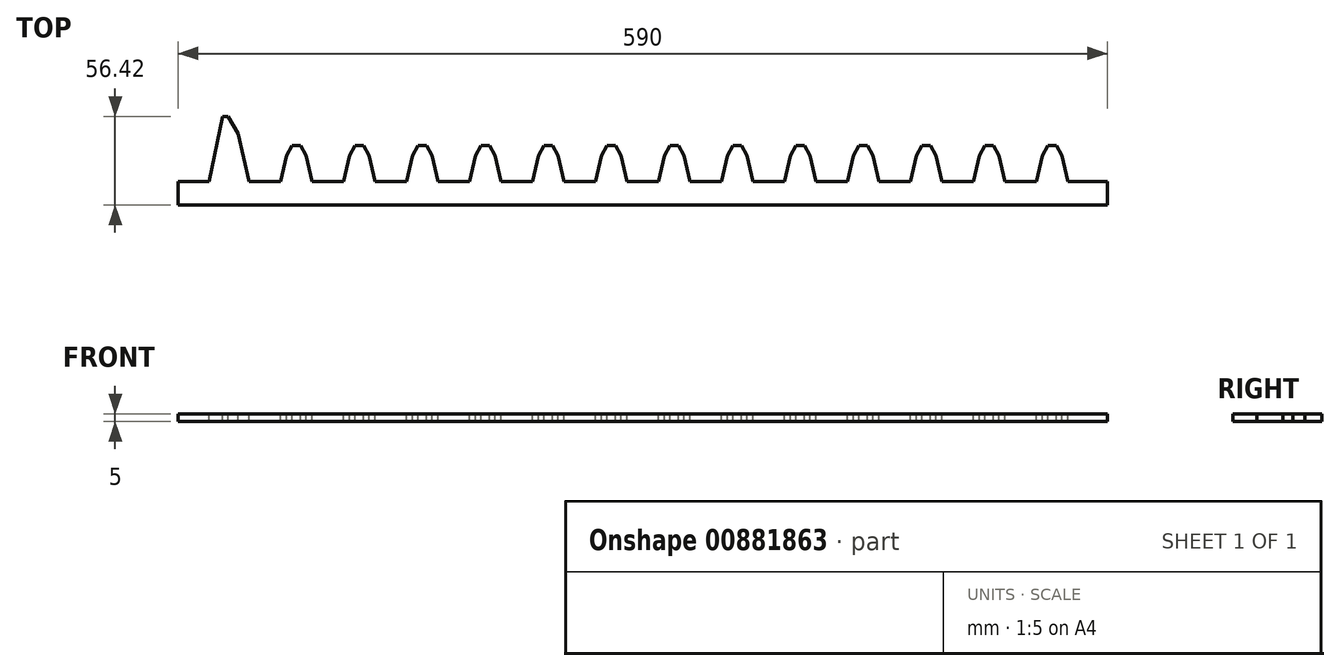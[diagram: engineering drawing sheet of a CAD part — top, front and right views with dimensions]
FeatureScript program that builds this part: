
annotation { "Feature Type Name" : "Feature", "Feature Type Description" : "" }
export const myFeature = defineFeature(function(context is Context, id is Id, definition is map)
    precondition{}
    {
        {
            var Q0;
            Q0=qCreatedBy(makeId("Top.planeOp"),FACE);
            var sketch = newSketch(context, id + "F0", { "sketchPlane" : qUnion([Q0])});
            skLineSegment(sketch, "E0.bottom", {"start": v(375, -330) * mm, "end": v(-375, -330) * mm});
            skLineSegment(sketch, "E0.top", {"start": v(375, 330) * mm, "end": v(-375, 330) * mm});
            skLineSegment(sketch, "E0.left", {"start": v(375, -330) * mm, "end": v(375, -280) * mm});
            skLineSegment(sketch, "E0.right", {"start": v(-375, -330) * mm, "end": v(-375, -280) * mm});
            skPoint(sketch, "E0.middle", {"position": v(0, 0) * mm});
            skLineSegment(sketch, "E1", {"start": v(-375, 280) * mm, "end": v(375, 280) * mm});
            skLineSegment(sketch, "E2", {"start": v(-375, -280) * mm, "end": v(375, -280) * mm});
            skLineSegment(sketch, "E3.trimOffspring", {"start": v(-375, 280) * mm, "end": v(-375, 330) * mm});
            skLineSegment(sketch, "E4.trimOffspring", {"start": v(375, 280) * mm, "end": v(375, 330) * mm});
            skSolve(sketch);
        }
        {
            var Q0;
            Q0=qSketchRegion(id+"F0",true);
            extrude(context, id + "F1", {"entities" : qUnion([Q0]), "depth" : 20 * mm, "offsetDistance" : 25 * mm});
        }
        {
            var Q0;
            Q0=makeQuery(id+"F1.opExtrude","CAP_FACE",FACE,{"disambiguationData":[OSD([sQuery(id+"F0.wireOp",EDGE,"E0.bottom"),sQuery(id+"F0.wireOp",EDGE,"E0.left"),sQuery(id+"F0.wireOp",EDGE,"E0.right"),sQuery(id+"F0.wireOp",EDGE,"E2")])],"isStart":false});
            var sketch = newSketch(context, id + "F2", { "sketchPlane" : qUnion([Q0])});
            skLineSegment(sketch, "E5", {"start": v(0, 349.99) * mm, "end": v(0, -330) * mm, "construction": true});
            skLineSegment(sketch, "E6.bottom", {"start": v(-362.1, -330) * mm, "end": v(-312.1, -330) * mm});
            skLineSegment(sketch, "E6.top", {"start": v(-362.1, 330) * mm, "end": v(-312.1, 330) * mm});
            skLineSegment(sketch, "E6.left", {"start": v(-362.1, -330) * mm, "end": v(-362.1, 330) * mm});
            skLineSegment(sketch, "E6.right", {"start": v(-312.1, -330) * mm, "end": v(-312.1, 330) * mm});
            skLineSegment(sketch, "E7.MirrorCS", {"start": v(312.1, -330) * mm, "end": v(312.1, 330) * mm});
            skLineSegment(sketch, "E8.MirrorCS", {"start": v(362.1, 330) * mm, "end": v(312.1, 330) * mm});
            skLineSegment(sketch, "E9.MirrorCS", {"start": v(362.1, -330) * mm, "end": v(362.1, 330) * mm});
            skLineSegment(sketch, "E10.MirrorCS", {"start": v(362.1, -330) * mm, "end": v(312.1, -330) * mm});
            skLineSegment(sketch, "E11.bottom", {"start": v(-105.33, -330) * mm, "end": v(-155.33, -330) * mm});
            skLineSegment(sketch, "E11.top", {"start": v(-105.33, 330) * mm, "end": v(-155.33, 330) * mm});
            skLineSegment(sketch, "E11.left", {"start": v(-105.33, -330) * mm, "end": v(-105.33, 330) * mm});
            skLineSegment(sketch, "E11.right", {"start": v(-155.33, -330) * mm, "end": v(-155.33, 330) * mm});
            skPoint(sketch, "E11.middle", {"position": v(-130.33, 0) * mm});
            skLineSegment(sketch, "E12.MirrorCS", {"start": v(105.33, -330) * mm, "end": v(105.33, 330) * mm});
            skLineSegment(sketch, "E13.MirrorCS", {"start": v(105.33, 330) * mm, "end": v(155.33, 330) * mm});
            skLineSegment(sketch, "E14.MirrorCS", {"start": v(155.33, -330) * mm, "end": v(155.33, 330) * mm});
            skLineSegment(sketch, "E15.MirrorCS", {"start": v(105.33, -330) * mm, "end": v(155.33, -330) * mm});
            skSolve(sketch);
        }
        {
            var Q0;
            Q0=qSketchRegion(id+"F2",true);
            extrude(context, id + "F3", {"entities" : qUnion([Q0]), "depth" : 10 * mm, "offsetDistance" : 25 * mm});
        }
        {
            var Q0;
            {var subQ2=sQuery(id+"F2.wireOp",EDGE,"E6.right");var subQ3=sQuery(id+"F0.wireOp",EDGE,"E2");var subQ4=sQuery(id+"F0.wireOp",EDGE,"E0.bottom");Q0=makeQuery(id+"F3.boolean.opBoolean","SPLIT",FACE,{"disambiguationData":[TD([makeQuery(id+"F3.opExtrude","SWEPT_FACE",FACE,{"disambiguationData":[OSD([subQ2])]})])],"derivedFrom":makeQuery(id+"F1.opExtrude","CAP_FACE",FACE,{"disambiguationData":[OSD([subQ4,sQuery(id+"F0.wireOp",EDGE,"E0.left"),sQuery(id+"F0.wireOp",EDGE,"E0.right"),subQ3])],"isStart":false})});}
            var sketch = newSketch(context, id + "F4", { "sketchPlane" : qUnion([Q0])});
            skLineSegment(sketch, "E16", {"start": v(0, -280) * mm, "end": v(0, 283.58) * mm, "construction": true});
            skLineSegment(sketch, "E17", {"start": v(265.2, 0) * mm, "end": v(-291.71, 0) * mm, "construction": true});
            skLineSegment(sketch, "E18", {"start": v(0, -280) * mm, "end": v(0, -429.27) * mm, "construction": true});
            skLineSegment(sketch, "E19", {"start": v(0, -429.27) * mm, "end": v(-300, -429.27) * mm, "construction": true});
            skLineSegment(sketch, "E20", {"start": v(-300, -429.27) * mm, "end": v(-300, -280) * mm, "construction": true});
            skLineSegment(sketch, "E21", {"start": v(-300, -280) * mm, "end": v(-296.16, -263.57) * mm});
            skLineSegment(sketch, "E22", {"start": v(-296.16, -263.57) * mm, "end": v(-292.67, -257.02) * mm});
            skLineSegment(sketch, "E23", {"start": v(-292.67, -257.02) * mm, "end": v(-290, -257.02) * mm});
            skLineSegment(sketch, "E24", {"start": v(-290, -257.02) * mm, "end": v(-290, -280) * mm, "construction": true});
            skLineSegment(sketch, "E25.MirrorCS", {"start": v(-287.33, -257.02) * mm, "end": v(-290, -257.02) * mm});
            skLineSegment(sketch, "E26.MirrorCS", {"start": v(-283.84, -263.57) * mm, "end": v(-287.33, -257.02) * mm});
            skLineSegment(sketch, "E27.MirrorCS", {"start": v(-280, -280) * mm, "end": v(-283.84, -263.57) * mm});
            skLineSegment(sketch, "E28.1.0.0", {"start": v(-260, -280) * mm, "end": v(-256.16, -263.57) * mm});
            skLineSegment(sketch, "E28.1.0.1", {"start": v(-256.16, -263.57) * mm, "end": v(-252.67, -257.02) * mm});
            skLineSegment(sketch, "E28.1.0.2", {"start": v(-252.67, -257.02) * mm, "end": v(-250, -257.02) * mm});
            skLineSegment(sketch, "E28.1.0.3", {"start": v(-247.33, -257.02) * mm, "end": v(-250, -257.02) * mm});
            skLineSegment(sketch, "E28.1.0.4", {"start": v(-243.84, -263.57) * mm, "end": v(-247.33, -257.02) * mm});
            skLineSegment(sketch, "E28.1.0.5", {"start": v(-240, -280) * mm, "end": v(-243.84, -263.57) * mm});
            skLineSegment(sketch, "E28.2.0.0", {"start": v(-220, -280) * mm, "end": v(-216.16, -263.57) * mm});
            skLineSegment(sketch, "E28.2.0.1", {"start": v(-216.16, -263.57) * mm, "end": v(-212.67, -257.02) * mm});
            skLineSegment(sketch, "E28.2.0.2", {"start": v(-212.67, -257.02) * mm, "end": v(-210, -257.02) * mm});
            skLineSegment(sketch, "E28.2.0.3", {"start": v(-207.33, -257.02) * mm, "end": v(-210, -257.02) * mm});
            skLineSegment(sketch, "E28.2.0.4", {"start": v(-203.84, -263.57) * mm, "end": v(-207.33, -257.02) * mm});
            skLineSegment(sketch, "E28.2.0.5", {"start": v(-200, -280) * mm, "end": v(-203.84, -263.57) * mm});
            skLineSegment(sketch, "E28.3.0.0", {"start": v(-180, -280) * mm, "end": v(-176.16, -263.57) * mm});
            skLineSegment(sketch, "E28.3.0.1", {"start": v(-176.16, -263.57) * mm, "end": v(-172.67, -257.02) * mm});
            skLineSegment(sketch, "E28.3.0.2", {"start": v(-172.67, -257.02) * mm, "end": v(-170, -257.02) * mm});
            skLineSegment(sketch, "E28.3.0.3", {"start": v(-167.33, -257.02) * mm, "end": v(-170, -257.02) * mm});
            skLineSegment(sketch, "E28.3.0.4", {"start": v(-163.84, -263.57) * mm, "end": v(-167.33, -257.02) * mm});
            skLineSegment(sketch, "E28.3.0.5", {"start": v(-160, -280) * mm, "end": v(-163.84, -263.57) * mm});
            skLineSegment(sketch, "E28.4.0.0", {"start": v(-140, -280) * mm, "end": v(-136.16, -263.57) * mm});
            skLineSegment(sketch, "E28.4.0.1", {"start": v(-136.16, -263.57) * mm, "end": v(-132.67, -257.02) * mm});
            skLineSegment(sketch, "E28.4.0.2", {"start": v(-132.67, -257.02) * mm, "end": v(-130, -257.02) * mm});
            skLineSegment(sketch, "E28.4.0.3", {"start": v(-127.33, -257.02) * mm, "end": v(-130, -257.02) * mm});
            skLineSegment(sketch, "E28.4.0.4", {"start": v(-123.84, -263.57) * mm, "end": v(-127.33, -257.02) * mm});
            skLineSegment(sketch, "E28.4.0.5", {"start": v(-120, -280) * mm, "end": v(-123.84, -263.57) * mm});
            skLineSegment(sketch, "E28.5.0.0", {"start": v(-100, -280) * mm, "end": v(-96.16, -263.57) * mm});
            skLineSegment(sketch, "E28.5.0.1", {"start": v(-96.16, -263.57) * mm, "end": v(-92.67, -257.02) * mm});
            skLineSegment(sketch, "E28.5.0.2", {"start": v(-92.67, -257.02) * mm, "end": v(-90, -257.02) * mm});
            skLineSegment(sketch, "E28.5.0.3", {"start": v(-87.33, -257.02) * mm, "end": v(-90, -257.02) * mm});
            skLineSegment(sketch, "E28.5.0.4", {"start": v(-83.84, -263.57) * mm, "end": v(-87.33, -257.02) * mm});
            skLineSegment(sketch, "E28.5.0.5", {"start": v(-80, -280) * mm, "end": v(-83.84, -263.57) * mm});
            skLineSegment(sketch, "E28.6.0.0", {"start": v(-60, -280) * mm, "end": v(-56.16, -263.57) * mm});
            skLineSegment(sketch, "E28.6.0.1", {"start": v(-56.16, -263.57) * mm, "end": v(-52.67, -257.02) * mm});
            skLineSegment(sketch, "E28.6.0.2", {"start": v(-52.67, -257.02) * mm, "end": v(-50, -257.02) * mm});
            skLineSegment(sketch, "E28.6.0.3", {"start": v(-47.33, -257.02) * mm, "end": v(-50, -257.02) * mm});
            skLineSegment(sketch, "E28.6.0.4", {"start": v(-43.84, -263.57) * mm, "end": v(-47.33, -257.02) * mm});
            skLineSegment(sketch, "E28.6.0.5", {"start": v(-40, -280) * mm, "end": v(-43.84, -263.57) * mm});
            skLineSegment(sketch, "E28.7.0.0", {"start": v(-20, -280) * mm, "end": v(-16.16, -263.57) * mm});
            skLineSegment(sketch, "E28.7.0.1", {"start": v(-16.16, -263.57) * mm, "end": v(-12.67, -257.02) * mm});
            skLineSegment(sketch, "E28.7.0.2", {"start": v(-12.67, -257.02) * mm, "end": v(-10, -257.02) * mm});
            skLineSegment(sketch, "E28.7.0.3", {"start": v(-7.33, -257.02) * mm, "end": v(-10, -257.02) * mm});
            skLineSegment(sketch, "E28.7.0.4", {"start": v(-3.84, -263.57) * mm, "end": v(-7.33, -257.02) * mm});
            skLineSegment(sketch, "E28.7.0.5", {"start": v(0, -280) * mm, "end": v(-3.84, -263.57) * mm});
            skLineSegment(sketch, "E28.8.0.0", {"start": v(20, -280) * mm, "end": v(23.84, -263.57) * mm});
            skLineSegment(sketch, "E28.8.0.1", {"start": v(23.84, -263.57) * mm, "end": v(27.33, -257.02) * mm});
            skLineSegment(sketch, "E28.8.0.2", {"start": v(27.33, -257.02) * mm, "end": v(30, -257.02) * mm});
            skLineSegment(sketch, "E28.8.0.3", {"start": v(32.67, -257.02) * mm, "end": v(30, -257.02) * mm});
            skLineSegment(sketch, "E28.8.0.4", {"start": v(36.16, -263.57) * mm, "end": v(32.67, -257.02) * mm});
            skLineSegment(sketch, "E28.8.0.5", {"start": v(40, -280) * mm, "end": v(36.16, -263.57) * mm});
            skLineSegment(sketch, "E28.9.0.0", {"start": v(60, -280) * mm, "end": v(63.84, -263.57) * mm});
            skLineSegment(sketch, "E28.9.0.1", {"start": v(63.84, -263.57) * mm, "end": v(67.33, -257.02) * mm});
            skLineSegment(sketch, "E28.9.0.2", {"start": v(67.33, -257.02) * mm, "end": v(70, -257.02) * mm});
            skLineSegment(sketch, "E28.9.0.3", {"start": v(72.67, -257.02) * mm, "end": v(70, -257.02) * mm});
            skLineSegment(sketch, "E28.9.0.4", {"start": v(76.16, -263.57) * mm, "end": v(72.67, -257.02) * mm});
            skLineSegment(sketch, "E28.9.0.5", {"start": v(80, -280) * mm, "end": v(76.16, -263.57) * mm});
            skLineSegment(sketch, "E28.10.0.0", {"start": v(100, -280) * mm, "end": v(103.84, -263.57) * mm});
            skLineSegment(sketch, "E28.10.0.1", {"start": v(103.84, -263.57) * mm, "end": v(107.33, -257.02) * mm});
            skLineSegment(sketch, "E28.10.0.2", {"start": v(107.33, -257.02) * mm, "end": v(110, -257.02) * mm});
            skLineSegment(sketch, "E28.10.0.3", {"start": v(112.67, -257.02) * mm, "end": v(110, -257.02) * mm});
            skLineSegment(sketch, "E28.10.0.4", {"start": v(116.16, -263.57) * mm, "end": v(112.67, -257.02) * mm});
            skLineSegment(sketch, "E28.10.0.5", {"start": v(120, -280) * mm, "end": v(116.16, -263.57) * mm});
            skLineSegment(sketch, "E28.11.0.0", {"start": v(140, -280) * mm, "end": v(143.84, -263.57) * mm});
            skLineSegment(sketch, "E28.11.0.1", {"start": v(143.84, -263.57) * mm, "end": v(147.33, -257.02) * mm});
            skLineSegment(sketch, "E28.11.0.2", {"start": v(147.33, -257.02) * mm, "end": v(150, -257.02) * mm});
            skLineSegment(sketch, "E28.11.0.3", {"start": v(152.67, -257.02) * mm, "end": v(150, -257.02) * mm});
            skLineSegment(sketch, "E28.11.0.4", {"start": v(156.16, -263.57) * mm, "end": v(152.67, -257.02) * mm});
            skLineSegment(sketch, "E28.11.0.5", {"start": v(160, -280) * mm, "end": v(156.16, -263.57) * mm});
            skLineSegment(sketch, "E28.12.0.0", {"start": v(180, -280) * mm, "end": v(183.84, -263.57) * mm});
            skLineSegment(sketch, "E28.12.0.1", {"start": v(183.84, -263.57) * mm, "end": v(187.33, -257.02) * mm});
            skLineSegment(sketch, "E28.12.0.2", {"start": v(187.33, -257.02) * mm, "end": v(190, -257.02) * mm});
            skLineSegment(sketch, "E28.12.0.3", {"start": v(192.67, -257.02) * mm, "end": v(190, -257.02) * mm});
            skLineSegment(sketch, "E28.12.0.4", {"start": v(196.16, -263.57) * mm, "end": v(192.67, -257.02) * mm});
            skLineSegment(sketch, "E28.12.0.5", {"start": v(200, -280) * mm, "end": v(196.16, -263.57) * mm});
            skLineSegment(sketch, "E28.13.0.0", {"start": v(220, -280) * mm, "end": v(223.84, -263.57) * mm});
            skLineSegment(sketch, "E28.13.0.1", {"start": v(223.84, -263.57) * mm, "end": v(227.33, -257.02) * mm});
            skLineSegment(sketch, "E28.13.0.2", {"start": v(227.33, -257.02) * mm, "end": v(230, -257.02) * mm});
            skLineSegment(sketch, "E28.13.0.3", {"start": v(232.67, -257.02) * mm, "end": v(230, -257.02) * mm});
            skLineSegment(sketch, "E28.13.0.4", {"start": v(236.16, -263.57) * mm, "end": v(232.67, -257.02) * mm});
            skLineSegment(sketch, "E28.13.0.5", {"start": v(240, -280) * mm, "end": v(236.16, -263.57) * mm});
            skLineSegment(sketch, "E28.direction1", {"start": v(-300, -280) * mm, "end": v(-260, -280) * mm, "construction": true});
            skLineSegment(sketch, "E29", {"start": v(-300, -280) * mm, "end": v(240, -280) * mm});
            skLineSegment(sketch, "E30.MirrorCS", {"start": v(-300, 280) * mm, "end": v(-296.16, 263.57) * mm});
            skLineSegment(sketch, "E31.MirrorCS", {"start": v(-296.16, 263.57) * mm, "end": v(-292.67, 257.02) * mm});
            skLineSegment(sketch, "E32.MirrorCS", {"start": v(-292.67, 257.02) * mm, "end": v(-290, 257.02) * mm});
            skLineSegment(sketch, "E33.MirrorCS", {"start": v(-287.33, 257.02) * mm, "end": v(-290, 257.02) * mm});
            skLineSegment(sketch, "E34.MirrorCS", {"start": v(-283.84, 263.57) * mm, "end": v(-287.33, 257.02) * mm});
            skLineSegment(sketch, "E35.MirrorCS", {"start": v(-280, 280) * mm, "end": v(-283.84, 263.57) * mm});
            skLineSegment(sketch, "E36.MirrorCS", {"start": v(-300, 280) * mm, "end": v(240, 280) * mm});
            skLineSegment(sketch, "E37.1.0.0", {"start": v(-260, 280) * mm, "end": v(-256.16, 263.57) * mm});
            skLineSegment(sketch, "E37.1.0.1", {"start": v(-256.16, 263.57) * mm, "end": v(-252.67, 257.02) * mm});
            skLineSegment(sketch, "E37.1.0.2", {"start": v(-252.67, 257.02) * mm, "end": v(-250, 257.02) * mm});
            skLineSegment(sketch, "E37.1.0.3", {"start": v(-247.33, 257.02) * mm, "end": v(-250, 257.02) * mm});
            skLineSegment(sketch, "E37.1.0.4", {"start": v(-243.84, 263.57) * mm, "end": v(-247.33, 257.02) * mm});
            skLineSegment(sketch, "E37.1.0.5", {"start": v(-240, 280) * mm, "end": v(-243.84, 263.57) * mm});
            skLineSegment(sketch, "E37.2.0.0", {"start": v(-220, 280) * mm, "end": v(-216.16, 263.57) * mm});
            skLineSegment(sketch, "E37.2.0.1", {"start": v(-216.16, 263.57) * mm, "end": v(-212.67, 257.02) * mm});
            skLineSegment(sketch, "E37.2.0.2", {"start": v(-212.67, 257.02) * mm, "end": v(-210, 257.02) * mm});
            skLineSegment(sketch, "E37.2.0.3", {"start": v(-207.33, 257.02) * mm, "end": v(-210, 257.02) * mm});
            skLineSegment(sketch, "E37.2.0.4", {"start": v(-203.84, 263.57) * mm, "end": v(-207.33, 257.02) * mm});
            skLineSegment(sketch, "E37.2.0.5", {"start": v(-200, 280) * mm, "end": v(-203.84, 263.57) * mm});
            skLineSegment(sketch, "E37.3.0.0", {"start": v(-180, 280) * mm, "end": v(-176.16, 263.57) * mm});
            skLineSegment(sketch, "E37.3.0.1", {"start": v(-176.16, 263.57) * mm, "end": v(-172.67, 257.02) * mm});
            skLineSegment(sketch, "E37.3.0.2", {"start": v(-172.67, 257.02) * mm, "end": v(-170, 257.02) * mm});
            skLineSegment(sketch, "E37.3.0.3", {"start": v(-167.33, 257.02) * mm, "end": v(-170, 257.02) * mm});
            skLineSegment(sketch, "E37.3.0.4", {"start": v(-163.84, 263.57) * mm, "end": v(-167.33, 257.02) * mm});
            skLineSegment(sketch, "E37.3.0.5", {"start": v(-160, 280) * mm, "end": v(-163.84, 263.57) * mm});
            skLineSegment(sketch, "E37.4.0.0", {"start": v(-140, 280) * mm, "end": v(-136.16, 263.57) * mm});
            skLineSegment(sketch, "E37.4.0.1", {"start": v(-136.16, 263.57) * mm, "end": v(-132.67, 257.02) * mm});
            skLineSegment(sketch, "E37.4.0.2", {"start": v(-132.67, 257.02) * mm, "end": v(-130, 257.02) * mm});
            skLineSegment(sketch, "E37.4.0.3", {"start": v(-127.33, 257.02) * mm, "end": v(-130, 257.02) * mm});
            skLineSegment(sketch, "E37.4.0.4", {"start": v(-123.84, 263.57) * mm, "end": v(-127.33, 257.02) * mm});
            skLineSegment(sketch, "E37.4.0.5", {"start": v(-120, 280) * mm, "end": v(-123.84, 263.57) * mm});
            skLineSegment(sketch, "E37.5.0.0", {"start": v(-100, 280) * mm, "end": v(-96.16, 263.57) * mm});
            skLineSegment(sketch, "E37.5.0.1", {"start": v(-96.16, 263.57) * mm, "end": v(-92.67, 257.02) * mm});
            skLineSegment(sketch, "E37.5.0.2", {"start": v(-92.67, 257.02) * mm, "end": v(-90, 257.02) * mm});
            skLineSegment(sketch, "E37.5.0.3", {"start": v(-87.33, 257.02) * mm, "end": v(-90, 257.02) * mm});
            skLineSegment(sketch, "E37.5.0.4", {"start": v(-83.84, 263.57) * mm, "end": v(-87.33, 257.02) * mm});
            skLineSegment(sketch, "E37.5.0.5", {"start": v(-80, 280) * mm, "end": v(-83.84, 263.57) * mm});
            skLineSegment(sketch, "E37.6.0.0", {"start": v(-60, 280) * mm, "end": v(-56.16, 263.57) * mm});
            skLineSegment(sketch, "E37.6.0.1", {"start": v(-56.16, 263.57) * mm, "end": v(-52.67, 257.02) * mm});
            skLineSegment(sketch, "E37.6.0.2", {"start": v(-52.67, 257.02) * mm, "end": v(-50, 257.02) * mm});
            skLineSegment(sketch, "E37.6.0.3", {"start": v(-47.33, 257.02) * mm, "end": v(-50, 257.02) * mm});
            skLineSegment(sketch, "E37.6.0.4", {"start": v(-43.84, 263.57) * mm, "end": v(-47.33, 257.02) * mm});
            skLineSegment(sketch, "E37.6.0.5", {"start": v(-40, 280) * mm, "end": v(-43.84, 263.57) * mm});
            skLineSegment(sketch, "E37.7.0.0", {"start": v(-20, 280) * mm, "end": v(-16.16, 263.57) * mm});
            skLineSegment(sketch, "E37.7.0.1", {"start": v(-16.16, 263.57) * mm, "end": v(-12.67, 257.02) * mm});
            skLineSegment(sketch, "E37.7.0.2", {"start": v(-12.67, 257.02) * mm, "end": v(-10, 257.02) * mm});
            skLineSegment(sketch, "E37.7.0.3", {"start": v(-7.33, 257.02) * mm, "end": v(-10, 257.02) * mm});
            skLineSegment(sketch, "E37.7.0.4", {"start": v(-3.84, 263.57) * mm, "end": v(-7.33, 257.02) * mm});
            skLineSegment(sketch, "E37.7.0.5", {"start": v(0, 280) * mm, "end": v(-3.84, 263.57) * mm});
            skLineSegment(sketch, "E37.8.0.0", {"start": v(20, 280) * mm, "end": v(23.84, 263.57) * mm});
            skLineSegment(sketch, "E37.8.0.1", {"start": v(23.84, 263.57) * mm, "end": v(27.33, 257.02) * mm});
            skLineSegment(sketch, "E37.8.0.2", {"start": v(27.33, 257.02) * mm, "end": v(30, 257.02) * mm});
            skLineSegment(sketch, "E37.8.0.3", {"start": v(32.67, 257.02) * mm, "end": v(30, 257.02) * mm});
            skLineSegment(sketch, "E37.8.0.4", {"start": v(36.16, 263.57) * mm, "end": v(32.67, 257.02) * mm});
            skLineSegment(sketch, "E37.8.0.5", {"start": v(40, 280) * mm, "end": v(36.16, 263.57) * mm});
            skLineSegment(sketch, "E37.9.0.0", {"start": v(60, 280) * mm, "end": v(63.84, 263.57) * mm});
            skLineSegment(sketch, "E37.9.0.1", {"start": v(63.84, 263.57) * mm, "end": v(67.33, 257.02) * mm});
            skLineSegment(sketch, "E37.9.0.2", {"start": v(67.33, 257.02) * mm, "end": v(70, 257.02) * mm});
            skLineSegment(sketch, "E37.9.0.3", {"start": v(72.67, 257.02) * mm, "end": v(70, 257.02) * mm});
            skLineSegment(sketch, "E37.9.0.4", {"start": v(76.16, 263.57) * mm, "end": v(72.67, 257.02) * mm});
            skLineSegment(sketch, "E37.9.0.5", {"start": v(80, 280) * mm, "end": v(76.16, 263.57) * mm});
            skLineSegment(sketch, "E37.10.0.0", {"start": v(100, 280) * mm, "end": v(103.84, 263.57) * mm});
            skLineSegment(sketch, "E37.10.0.1", {"start": v(103.84, 263.57) * mm, "end": v(107.33, 257.02) * mm});
            skLineSegment(sketch, "E37.10.0.2", {"start": v(107.33, 257.02) * mm, "end": v(110, 257.02) * mm});
            skLineSegment(sketch, "E37.10.0.3", {"start": v(112.67, 257.02) * mm, "end": v(110, 257.02) * mm});
            skLineSegment(sketch, "E37.10.0.4", {"start": v(116.16, 263.57) * mm, "end": v(112.67, 257.02) * mm});
            skLineSegment(sketch, "E37.10.0.5", {"start": v(120, 280) * mm, "end": v(116.16, 263.57) * mm});
            skLineSegment(sketch, "E37.11.0.0", {"start": v(140, 280) * mm, "end": v(143.84, 263.57) * mm});
            skLineSegment(sketch, "E37.11.0.1", {"start": v(143.84, 263.57) * mm, "end": v(147.33, 257.02) * mm});
            skLineSegment(sketch, "E37.11.0.2", {"start": v(147.33, 257.02) * mm, "end": v(150, 257.02) * mm});
            skLineSegment(sketch, "E37.11.0.3", {"start": v(152.67, 257.02) * mm, "end": v(150, 257.02) * mm});
            skLineSegment(sketch, "E37.11.0.4", {"start": v(156.16, 263.57) * mm, "end": v(152.67, 257.02) * mm});
            skLineSegment(sketch, "E37.11.0.5", {"start": v(160, 280) * mm, "end": v(156.16, 263.57) * mm});
            skLineSegment(sketch, "E37.12.0.0", {"start": v(180, 280) * mm, "end": v(183.84, 263.57) * mm});
            skLineSegment(sketch, "E37.12.0.1", {"start": v(183.84, 263.57) * mm, "end": v(187.33, 257.02) * mm});
            skLineSegment(sketch, "E37.12.0.2", {"start": v(187.33, 257.02) * mm, "end": v(190, 257.02) * mm});
            skLineSegment(sketch, "E37.12.0.3", {"start": v(192.67, 257.02) * mm, "end": v(190, 257.02) * mm});
            skLineSegment(sketch, "E37.12.0.4", {"start": v(196.16, 263.57) * mm, "end": v(192.67, 257.02) * mm});
            skLineSegment(sketch, "E37.12.0.5", {"start": v(200, 280) * mm, "end": v(196.16, 263.57) * mm});
            skLineSegment(sketch, "E37.13.0.0", {"start": v(220, 280) * mm, "end": v(223.84, 263.57) * mm});
            skLineSegment(sketch, "E37.13.0.1", {"start": v(223.84, 263.57) * mm, "end": v(227.33, 257.02) * mm});
            skLineSegment(sketch, "E37.13.0.2", {"start": v(227.33, 257.02) * mm, "end": v(230, 257.02) * mm});
            skLineSegment(sketch, "E37.13.0.3", {"start": v(232.67, 257.02) * mm, "end": v(230, 257.02) * mm});
            skLineSegment(sketch, "E37.13.0.4", {"start": v(236.16, 263.57) * mm, "end": v(232.67, 257.02) * mm});
            skLineSegment(sketch, "E37.13.0.5", {"start": v(240, 280) * mm, "end": v(236.16, 263.57) * mm});
            skLineSegment(sketch, "E37.direction1", {"start": v(-296.16, 263.57) * mm, "end": v(-256.16, 263.57) * mm, "construction": true});
            skLineSegment(sketch, "E38", {"start": v(240, -280) * mm, "end": v(265, -280) * mm});
            skLineSegment(sketch, "E39", {"start": v(265, -280) * mm, "end": v(265, -295) * mm});
            skLineSegment(sketch, "E40", {"start": v(265, -295) * mm, "end": v(-325, -295) * mm});
            skLineSegment(sketch, "E41", {"start": v(-325, -295) * mm, "end": v(-325, -280) * mm});
            skLineSegment(sketch, "E42", {"start": v(-325, -280) * mm, "end": v(-300, -280) * mm});
            skLineSegment(sketch, "E43", {"start": v(-300, 280) * mm, "end": v(-325, 280) * mm});
            skLineSegment(sketch, "E44", {"start": v(-325, 280) * mm, "end": v(-325, 305) * mm});
            skLineSegment(sketch, "E45", {"start": v(-325, 305) * mm, "end": v(265, 305) * mm});
            skLineSegment(sketch, "E46", {"start": v(265, 305) * mm, "end": v(265, 280) * mm});
            skLineSegment(sketch, "E47", {"start": v(265, 280) * mm, "end": v(240, 280) * mm});
            skSolve(sketch);
        }
        {
            var Q0;
            Q0=qSketchRegion(id+"F4",true);
            extrude(context, id + "F5", {"entities" : qUnion([Q0]), "oppositeDirection" : true, "depth" : 5 * mm, "offsetDistance" : 25 * mm});
        }
        {
            var Q0;
            Q0=makeQuery(id+"F3.opExtrude","SWEPT_BODY",BODY,{"disambiguationData":[OSD([sQuery(id+"F2.wireOp",EDGE,"E7.MirrorCS"),sQuery(id+"F2.wireOp",EDGE,"E8.MirrorCS"),sQuery(id+"F2.wireOp",EDGE,"E9.MirrorCS"),sQuery(id+"F2.wireOp",EDGE,"E10.MirrorCS")])]});
            var Q1;
            Q1=makeQuery(id+"F3.opExtrude","SWEPT_BODY",BODY,{"disambiguationData":[OSD([sQuery(id+"F2.wireOp",EDGE,"E12.MirrorCS"),sQuery(id+"F2.wireOp",EDGE,"E13.MirrorCS"),sQuery(id+"F2.wireOp",EDGE,"E14.MirrorCS"),sQuery(id+"F2.wireOp",EDGE,"E15.MirrorCS")])]});
            var Q2;
            Q2=makeQuery(id+"F3.opExtrude","SWEPT_BODY",BODY,{"disambiguationData":[OSD([sQuery(id+"F2.wireOp",EDGE,"E11.bottom"),sQuery(id+"F2.wireOp",EDGE,"E11.top"),sQuery(id+"F2.wireOp",EDGE,"E11.left"),sQuery(id+"F2.wireOp",EDGE,"E11.right")])]});
            var Q3;
            Q3=makeQuery(id+"F3.opExtrude","SWEPT_BODY",BODY,{"disambiguationData":[OSD([sQuery(id+"F2.wireOp",EDGE,"E6.bottom"),sQuery(id+"F2.wireOp",EDGE,"E6.top"),sQuery(id+"F2.wireOp",EDGE,"E6.left"),sQuery(id+"F2.wireOp",EDGE,"E6.right")])]});
            var Q4;
            Q4=makeQuery(id+"F1.opExtrude","SWEPT_BODY",BODY,{"disambiguationData":[OSD([sQuery(id+"F0.wireOp",EDGE,"E0.bottom"),sQuery(id+"F0.wireOp",EDGE,"E0.left"),sQuery(id+"F0.wireOp",EDGE,"E0.right"),sQuery(id+"F0.wireOp",EDGE,"E2")])]});
            var Q5;
            Q5=makeQuery(id+"F1.opExtrude","SWEPT_BODY",BODY,{"disambiguationData":[OSD([sQuery(id+"F0.wireOp",EDGE,"E0.top"),sQuery(id+"F0.wireOp",EDGE,"E1"),sQuery(id+"F0.wireOp",EDGE,"E3.trimOffspring"),sQuery(id+"F0.wireOp",EDGE,"E4.trimOffspring")])]});
            deleteBodies(context, id + "F6", {"entities" : qUnion([Q0, Q1, Q2, Q3, Q4, Q5])});
        }
        {
            var Q0;
            Q0=makeQuery(id+"F5.opExtrude","SWEPT_BODY",BODY,{"disambiguationData":[OSD([sQuery(id+"F4.wireOp",EDGE,"E30.MirrorCS"),sQuery(id+"F4.wireOp",EDGE,"E31.MirrorCS"),sQuery(id+"F4.wireOp",EDGE,"E32.MirrorCS"),sQuery(id+"F4.wireOp",EDGE,"E33.MirrorCS"),sQuery(id+"F4.wireOp",EDGE,"E34.MirrorCS"),sQuery(id+"F4.wireOp",EDGE,"E35.MirrorCS"),sQuery(id+"F4.wireOp",EDGE,"E36.MirrorCS"),sQuery(id+"F4.wireOp",EDGE,"E37.1.0.0"),sQuery(id+"F4.wireOp",EDGE,"E37.1.0.1"),sQuery(id+"F4.wireOp",EDGE,"E37.1.0.2"),sQuery(id+"F4.wireOp",EDGE,"E37.1.0.3"),sQuery(id+"F4.wireOp",EDGE,"E37.1.0.4"),sQuery(id+"F4.wireOp",EDGE,"E37.1.0.5"),sQuery(id+"F4.wireOp",EDGE,"E37.2.0.0"),sQuery(id+"F4.wireOp",EDGE,"E37.2.0.1"),sQuery(id+"F4.wireOp",EDGE,"E37.2.0.2"),sQuery(id+"F4.wireOp",EDGE,"E37.2.0.3"),sQuery(id+"F4.wireOp",EDGE,"E37.2.0.4"),sQuery(id+"F4.wireOp",EDGE,"E37.2.0.5"),sQuery(id+"F4.wireOp",EDGE,"E37.3.0.0"),sQuery(id+"F4.wireOp",EDGE,"E37.3.0.1"),sQuery(id+"F4.wireOp",EDGE,"E37.3.0.2"),sQuery(id+"F4.wireOp",EDGE,"E37.3.0.3"),sQuery(id+"F4.wireOp",EDGE,"E37.3.0.4"),sQuery(id+"F4.wireOp",EDGE,"E37.3.0.5"),sQuery(id+"F4.wireOp",EDGE,"E37.4.0.0"),sQuery(id+"F4.wireOp",EDGE,"E37.4.0.1"),sQuery(id+"F4.wireOp",EDGE,"E37.4.0.2"),sQuery(id+"F4.wireOp",EDGE,"E37.4.0.3"),sQuery(id+"F4.wireOp",EDGE,"E37.4.0.4"),sQuery(id+"F4.wireOp",EDGE,"E37.4.0.5"),sQuery(id+"F4.wireOp",EDGE,"E37.5.0.0"),sQuery(id+"F4.wireOp",EDGE,"E37.5.0.1"),sQuery(id+"F4.wireOp",EDGE,"E37.5.0.2"),sQuery(id+"F4.wireOp",EDGE,"E37.5.0.3"),sQuery(id+"F4.wireOp",EDGE,"E37.5.0.4"),sQuery(id+"F4.wireOp",EDGE,"E37.5.0.5"),sQuery(id+"F4.wireOp",EDGE,"E37.6.0.0"),sQuery(id+"F4.wireOp",EDGE,"E37.6.0.1"),sQuery(id+"F4.wireOp",EDGE,"E37.6.0.2"),sQuery(id+"F4.wireOp",EDGE,"E37.6.0.3"),sQuery(id+"F4.wireOp",EDGE,"E37.6.0.4"),sQuery(id+"F4.wireOp",EDGE,"E37.6.0.5"),sQuery(id+"F4.wireOp",EDGE,"E37.7.0.0"),sQuery(id+"F4.wireOp",EDGE,"E37.7.0.1"),sQuery(id+"F4.wireOp",EDGE,"E37.7.0.2"),sQuery(id+"F4.wireOp",EDGE,"E37.7.0.3"),sQuery(id+"F4.wireOp",EDGE,"E37.7.0.4"),sQuery(id+"F4.wireOp",EDGE,"E37.7.0.5"),sQuery(id+"F4.wireOp",EDGE,"E37.8.0.0"),sQuery(id+"F4.wireOp",EDGE,"E37.8.0.1"),sQuery(id+"F4.wireOp",EDGE,"E37.8.0.2"),sQuery(id+"F4.wireOp",EDGE,"E37.8.0.3"),sQuery(id+"F4.wireOp",EDGE,"E37.8.0.4"),sQuery(id+"F4.wireOp",EDGE,"E37.8.0.5"),sQuery(id+"F4.wireOp",EDGE,"E37.9.0.0"),sQuery(id+"F4.wireOp",EDGE,"E37.9.0.1"),sQuery(id+"F4.wireOp",EDGE,"E37.9.0.2"),sQuery(id+"F4.wireOp",EDGE,"E37.9.0.3"),sQuery(id+"F4.wireOp",EDGE,"E37.9.0.4"),sQuery(id+"F4.wireOp",EDGE,"E37.9.0.5"),sQuery(id+"F4.wireOp",EDGE,"E37.10.0.0"),sQuery(id+"F4.wireOp",EDGE,"E37.10.0.1"),sQuery(id+"F4.wireOp",EDGE,"E37.10.0.2"),sQuery(id+"F4.wireOp",EDGE,"E37.10.0.3"),sQuery(id+"F4.wireOp",EDGE,"E37.10.0.4"),sQuery(id+"F4.wireOp",EDGE,"E37.10.0.5"),sQuery(id+"F4.wireOp",EDGE,"E37.11.0.0"),sQuery(id+"F4.wireOp",EDGE,"E37.11.0.1"),sQuery(id+"F4.wireOp",EDGE,"E37.11.0.2"),sQuery(id+"F4.wireOp",EDGE,"E37.11.0.3"),sQuery(id+"F4.wireOp",EDGE,"E37.11.0.4"),sQuery(id+"F4.wireOp",EDGE,"E37.11.0.5"),sQuery(id+"F4.wireOp",EDGE,"E37.12.0.0"),sQuery(id+"F4.wireOp",EDGE,"E37.12.0.1"),sQuery(id+"F4.wireOp",EDGE,"E37.12.0.2"),sQuery(id+"F4.wireOp",EDGE,"E37.12.0.3"),sQuery(id+"F4.wireOp",EDGE,"E37.12.0.4"),sQuery(id+"F4.wireOp",EDGE,"E37.12.0.5"),sQuery(id+"F4.wireOp",EDGE,"E37.13.0.0"),sQuery(id+"F4.wireOp",EDGE,"E37.13.0.1"),sQuery(id+"F4.wireOp",EDGE,"E37.13.0.2"),sQuery(id+"F4.wireOp",EDGE,"E37.13.0.3"),sQuery(id+"F4.wireOp",EDGE,"E37.13.0.4"),sQuery(id+"F4.wireOp",EDGE,"E37.13.0.5"),sQuery(id+"F4.wireOp",EDGE,"E43"),sQuery(id+"F4.wireOp",EDGE,"E44"),sQuery(id+"F4.wireOp",EDGE,"E45"),sQuery(id+"F4.wireOp",EDGE,"E46"),sQuery(id+"F4.wireOp",EDGE,"E47")])]});
            deleteBodies(context, id + "F7", {"entities" : qUnion([Q0])});
        }
        {
            var Q0;
            Q0=makeQuery(id+"F5.opExtrude","CAP_FACE",FACE,{"disambiguationData":[OSD([sQuery(id+"F4.wireOp",EDGE,"E21"),sQuery(id+"F4.wireOp",EDGE,"E22"),sQuery(id+"F4.wireOp",EDGE,"E23"),sQuery(id+"F4.wireOp",EDGE,"E25.MirrorCS"),sQuery(id+"F4.wireOp",EDGE,"E26.MirrorCS"),sQuery(id+"F4.wireOp",EDGE,"E27.MirrorCS"),sQuery(id+"F4.wireOp",EDGE,"E28.1.0.0"),sQuery(id+"F4.wireOp",EDGE,"E28.1.0.1"),sQuery(id+"F4.wireOp",EDGE,"E28.1.0.2"),sQuery(id+"F4.wireOp",EDGE,"E28.1.0.3"),sQuery(id+"F4.wireOp",EDGE,"E28.1.0.4"),sQuery(id+"F4.wireOp",EDGE,"E28.1.0.5"),sQuery(id+"F4.wireOp",EDGE,"E28.2.0.0"),sQuery(id+"F4.wireOp",EDGE,"E28.2.0.1"),sQuery(id+"F4.wireOp",EDGE,"E28.2.0.2"),sQuery(id+"F4.wireOp",EDGE,"E28.2.0.3"),sQuery(id+"F4.wireOp",EDGE,"E28.2.0.4"),sQuery(id+"F4.wireOp",EDGE,"E28.2.0.5"),sQuery(id+"F4.wireOp",EDGE,"E28.3.0.0"),sQuery(id+"F4.wireOp",EDGE,"E28.3.0.1"),sQuery(id+"F4.wireOp",EDGE,"E28.3.0.2"),sQuery(id+"F4.wireOp",EDGE,"E28.3.0.3"),sQuery(id+"F4.wireOp",EDGE,"E28.3.0.4"),sQuery(id+"F4.wireOp",EDGE,"E28.3.0.5"),sQuery(id+"F4.wireOp",EDGE,"E28.4.0.0"),sQuery(id+"F4.wireOp",EDGE,"E28.4.0.1"),sQuery(id+"F4.wireOp",EDGE,"E28.4.0.2"),sQuery(id+"F4.wireOp",EDGE,"E28.4.0.3"),sQuery(id+"F4.wireOp",EDGE,"E28.4.0.4"),sQuery(id+"F4.wireOp",EDGE,"E28.4.0.5"),sQuery(id+"F4.wireOp",EDGE,"E28.5.0.0"),sQuery(id+"F4.wireOp",EDGE,"E28.5.0.1"),sQuery(id+"F4.wireOp",EDGE,"E28.5.0.2"),sQuery(id+"F4.wireOp",EDGE,"E28.5.0.3"),sQuery(id+"F4.wireOp",EDGE,"E28.5.0.4"),sQuery(id+"F4.wireOp",EDGE,"E28.5.0.5"),sQuery(id+"F4.wireOp",EDGE,"E28.6.0.0"),sQuery(id+"F4.wireOp",EDGE,"E28.6.0.1"),sQuery(id+"F4.wireOp",EDGE,"E28.6.0.2"),sQuery(id+"F4.wireOp",EDGE,"E28.6.0.3"),sQuery(id+"F4.wireOp",EDGE,"E28.6.0.4"),sQuery(id+"F4.wireOp",EDGE,"E28.6.0.5"),sQuery(id+"F4.wireOp",EDGE,"E28.7.0.0"),sQuery(id+"F4.wireOp",EDGE,"E28.7.0.1"),sQuery(id+"F4.wireOp",EDGE,"E28.7.0.2"),sQuery(id+"F4.wireOp",EDGE,"E28.7.0.3"),sQuery(id+"F4.wireOp",EDGE,"E28.7.0.4"),sQuery(id+"F4.wireOp",EDGE,"E28.7.0.5"),sQuery(id+"F4.wireOp",EDGE,"E28.8.0.0"),sQuery(id+"F4.wireOp",EDGE,"E28.8.0.1"),sQuery(id+"F4.wireOp",EDGE,"E28.8.0.2"),sQuery(id+"F4.wireOp",EDGE,"E28.8.0.3"),sQuery(id+"F4.wireOp",EDGE,"E28.8.0.4"),sQuery(id+"F4.wireOp",EDGE,"E28.8.0.5"),sQuery(id+"F4.wireOp",EDGE,"E28.9.0.0"),sQuery(id+"F4.wireOp",EDGE,"E28.9.0.1"),sQuery(id+"F4.wireOp",EDGE,"E28.9.0.2"),sQuery(id+"F4.wireOp",EDGE,"E28.9.0.3"),sQuery(id+"F4.wireOp",EDGE,"E28.9.0.4"),sQuery(id+"F4.wireOp",EDGE,"E28.9.0.5"),sQuery(id+"F4.wireOp",EDGE,"E28.10.0.0"),sQuery(id+"F4.wireOp",EDGE,"E28.10.0.1"),sQuery(id+"F4.wireOp",EDGE,"E28.10.0.2"),sQuery(id+"F4.wireOp",EDGE,"E28.10.0.3"),sQuery(id+"F4.wireOp",EDGE,"E28.10.0.4"),sQuery(id+"F4.wireOp",EDGE,"E28.10.0.5"),sQuery(id+"F4.wireOp",EDGE,"E28.11.0.0"),sQuery(id+"F4.wireOp",EDGE,"E28.11.0.1"),sQuery(id+"F4.wireOp",EDGE,"E28.11.0.2"),sQuery(id+"F4.wireOp",EDGE,"E28.11.0.3"),sQuery(id+"F4.wireOp",EDGE,"E28.11.0.4"),sQuery(id+"F4.wireOp",EDGE,"E28.11.0.5"),sQuery(id+"F4.wireOp",EDGE,"E28.12.0.0"),sQuery(id+"F4.wireOp",EDGE,"E28.12.0.1"),sQuery(id+"F4.wireOp",EDGE,"E28.12.0.2"),sQuery(id+"F4.wireOp",EDGE,"E28.12.0.3"),sQuery(id+"F4.wireOp",EDGE,"E28.12.0.4"),sQuery(id+"F4.wireOp",EDGE,"E28.12.0.5"),sQuery(id+"F4.wireOp",EDGE,"E28.13.0.0"),sQuery(id+"F4.wireOp",EDGE,"E28.13.0.1"),sQuery(id+"F4.wireOp",EDGE,"E28.13.0.2"),sQuery(id+"F4.wireOp",EDGE,"E28.13.0.3"),sQuery(id+"F4.wireOp",EDGE,"E28.13.0.4"),sQuery(id+"F4.wireOp",EDGE,"E28.13.0.5"),sQuery(id+"F4.wireOp",EDGE,"E29"),sQuery(id+"F4.wireOp",EDGE,"E38"),sQuery(id+"F4.wireOp",EDGE,"E39"),sQuery(id+"F4.wireOp",EDGE,"E40"),sQuery(id+"F4.wireOp",EDGE,"E41"),sQuery(id+"F4.wireOp",EDGE,"E42")])],"isStart":true});
            var sketch = newSketch(context, id + "F8", { "sketchPlane" : qUnion([Q0])});
            skLineSegment(sketch, "E48", {"start": v(-287, -249.45) * mm, "end": v(-280, -280) * mm});
            skLineSegment(sketch, "E49", {"start": v(-287, -249.45) * mm, "end": v(-293.27, -238.58) * mm});
            skLineSegment(sketch, "E50", {"start": v(-293.27, -238.58) * mm, "end": v(-296.98, -238.58) * mm});
            skLineSegment(sketch, "E51", {"start": v(-296.98, -238.58) * mm, "end": v(-305.36, -280) * mm});
            skLineSegment(sketch, "E52", {"start": v(-305.36, -280) * mm, "end": v(-280, -280) * mm});
            skSolve(sketch);
        }
        {
            var Q0;
            Q0=qSketchRegion(id+"F8",true);
            extrude(context, id + "F9", {"entities" : qUnion([Q0]), "operationType" : NewBodyOperationType.ADD, "oppositeDirection" : true, "depth" : 5 * mm, "offsetDistance" : 25 * mm});
        }
    });
